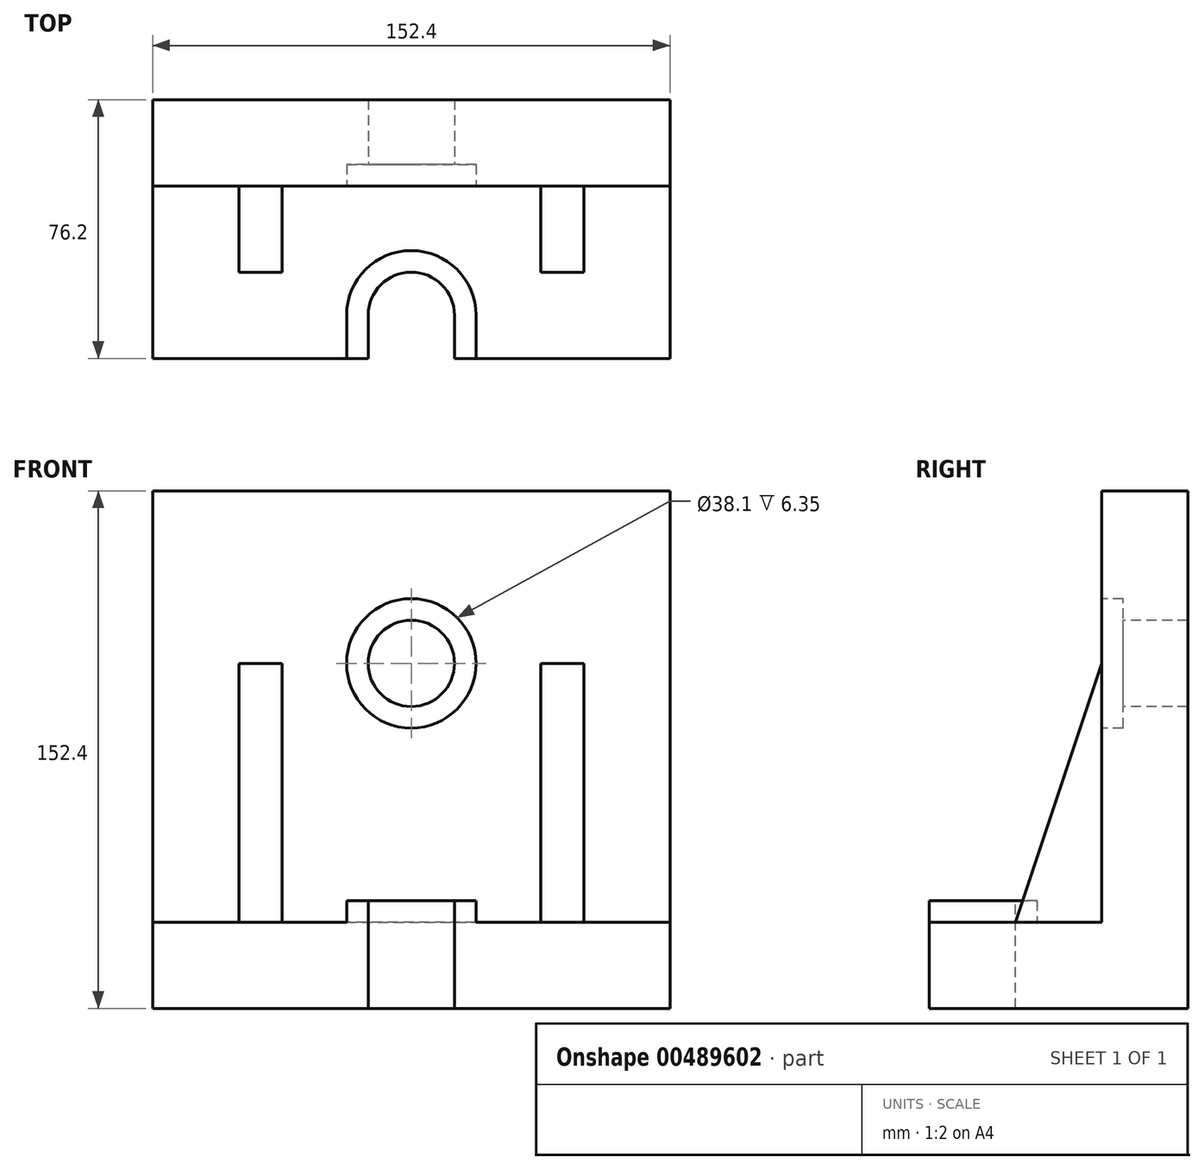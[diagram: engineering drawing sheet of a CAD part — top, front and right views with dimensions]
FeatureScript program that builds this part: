
annotation { "Feature Type Name" : "Feature", "Feature Type Description" : "" }
export const myFeature = defineFeature(function(context is Context, id is Id, definition is map)
    precondition{}
    {
        {
            var Q0;
            Q0=qCreatedBy(makeId("Right.planeOp"),FACE);
            var sketch = newSketch(context, id + "F0", { "sketchPlane" : qUnion([Q0])});
            skLineSegment(sketch, "E0", {"start": v(0, 0) * mm, "end": v(-76.2, 0) * mm});
            skLineSegment(sketch, "E1", {"start": v(-76.2, 0) * mm, "end": v(-76.2, 25.4) * mm});
            skLineSegment(sketch, "E2", {"start": v(-76.2, 25.4) * mm, "end": v(-25.4, 25.4) * mm});
            skLineSegment(sketch, "E3", {"start": v(-25.4, 25.4) * mm, "end": v(-25.4, 152.4) * mm});
            skLineSegment(sketch, "E4", {"start": v(-25.4, 152.4) * mm, "end": v(0, 152.4) * mm});
            skLineSegment(sketch, "E5", {"start": v(0, 152.4) * mm, "end": v(0, 0) * mm});
            skSolve(sketch);
        }
        {
            var Q0;
            Q0 = qSketchRegion(id + "F0", true);
            extrude(context, id + "F1", {"entities" : qUnion([Q0]), "endBound" : BoundingType.SYMMETRIC, "depth" : 152.4 * mm});
        }
        {
            var Q0;
            Q0=makeQuery(id+"F1.opExtrude","SWEPT_FACE",FACE,{"disambiguationData":[OSD([sQuery(id+"F0.wireOp",EDGE,"E2")])]});
            var sketch = newSketch(context, id + "F2", { "sketchPlane" : qUnion([Q0])});
            skArc(sketch, "E6", {"start": v(12.7, -63.5) * mm, "mid": v(0, -50.8) * mm, "end": v(-12.7, -63.5) * mm});
            skPoint(sketch, "E6.centerSnap0", {"position": v(0, -76.2) * mm});
            skLineSegment(sketch, "E7", {"start": v(-12.7, -63.5) * mm, "end": v(-12.7, -76.2) * mm});
            skLineSegment(sketch, "E8", {"start": v(12.7, -63.5) * mm, "end": v(12.7, -76.2) * mm});
            skSolve(sketch);
        }
        {
            var Q0;
            Q0 = qSketchRegion(id + "F2", true);
            var Q1;
            Q1=makeQuery(id+"F2.imprint","IMPRINT",FACE,{"disambiguationData":[TD([[makeQuery(id+"F2.imprint","IMPRINT",EDGE,{"derivedFrom":sQuery(id+"F2.wireOp",EDGE,"E6")}),1.0]])]});
            extrude(context, id + "F3", {"entities" : qUnion([Q0, Q1]), "operationType" : NewBodyOperationType.REMOVE, "endBound" : BoundingType.THROUGH_ALL, "oppositeDirection" : true, "depth" : 25.4 * mm});
        }
        {
            var Q0;
            Q0=makeQuery(id+"F1.opExtrude","SWEPT_FACE",FACE,{"disambiguationData":[OSD([sQuery(id+"F0.wireOp",EDGE,"E3")])]});
            var sketch = newSketch(context, id + "F4", { "sketchPlane" : qUnion([Q0])});
            skCircle(sketch, "E9", {"center": v(0, 101.6) * mm, "radius": 19.05 * mm});
            skCircle(sketch, "E10", {"center": v(0, 101.6) * mm, "radius": 12.7 * mm});
            skSolve(sketch);
        }
        {
            var Q0;
            Q0=makeQuery(id+"F4.imprint","IMPRINT",FACE,{"disambiguationData":[TD([[makeQuery(id+"F4.imprint","IMPRINT",EDGE,{"derivedFrom":sQuery(id+"F4.wireOp",EDGE,"E10")}),1.0]])]});
            extrude(context, id + "F5", {"entities" : qUnion([Q0]), "operationType" : NewBodyOperationType.REMOVE, "endBound" : BoundingType.THROUGH_ALL, "oppositeDirection" : true, "depth" : 25.4 * mm});
        }
        {
            var Q0;
            Q0=makeQuery(id+"F4.imprint","IMPRINT",FACE,{"disambiguationData":[TD([[makeQuery(id+"F4.imprint","IMPRINT",EDGE,{"derivedFrom":sQuery(id+"F4.wireOp",EDGE,"E9")}),1.0]])]});
            extrude(context, id + "F6", {"entities" : qUnion([Q0]), "operationType" : NewBodyOperationType.REMOVE, "oppositeDirection" : true, "depth" : 6.35 * mm});
        }
        {
            var Q0;
            Q0=qCreatedBy(makeId("Right.planeOp"),FACE);
            cPlane(context, id + "F7", {"entities" : qUnion([Q0]), "cplaneType" : CPlaneType.OFFSET, "offset" : 44.45 * mm, "width" : 152.4 * mm, "height" : 152.4 * mm});
        }
        {
            var Q0;
            Q0=qCreatedBy(id+"F7.planeOp",FACE);
            var sketch = newSketch(context, id + "F8", { "sketchPlane" : qUnion([Q0])});
            skLineSegment(sketch, "E11.0", {"start": v(-25.4, 25.4) * mm, "end": v(-25.4, 101.6) * mm});
            skLineSegment(sketch, "E12.0", {"start": v(-76.2, 25.4) * mm, "end": v(-25.4, 25.4) * mm});
            skLineSegment(sketch, "E13", {"start": v(-25.4, 101.6) * mm, "end": v(-50.8, 25.4) * mm});
            skLineSegment(sketch, "E14", {"start": v(-50.8, 25.4) * mm, "end": v(-25.4, 25.4) * mm});
            skSolve(sketch);
        }
        {
            var Q0;
            Q0 = qSketchRegion(id + "F8", true);
            extrude(context, id + "F9", {"entities" : qUnion([Q0]), "endBound" : BoundingType.SYMMETRIC, "depth" : 12.7 * mm});
        }
        {
            var Q0;
            Q0=makeQuery(id+"F9.opExtrude","SWEPT_BODY",BODY,{"disambiguationData":[OSD([sQuery(id+"F8.wireOp",EDGE,"E11.0"),sQuery(id+"F8.wireOp",EDGE,"E13"),sQuery(id+"F8.wireOp",EDGE,"E14")])]});
            var Q1;
            Q1=qCreatedBy(makeId("Right.planeOp"),FACE);
            mirror(context, id + "F10", {"operationType" : NewBodyOperationType.ADD, "entities" : qUnion([Q0]), "mirrorPlane" : qUnion([Q1])});
        }
        {
            var Q0;
            {var subQ2=sQuery(id+"F0.wireOp",EDGE,"E1");Q0=makeQuery(id+"F3.boolean.opBoolean","SPLIT",FACE,{"disambiguationData":[TD([makeQuery(id+"F3.opExtrude","SWEPT_FACE",FACE,{"disambiguationData":[OSD([sQuery(id+"F2.wireOp",EDGE,"E7")])]})])],"derivedFrom":makeQuery(id+"F1.opExtrude","SWEPT_FACE",FACE,{"disambiguationData":[OSD([subQ2])]})});}
            var sketch = newSketch(context, id + "F11", { "sketchPlane" : qUnion([Q0])});
            skLineSegment(sketch, "E15.bottom", {"start": v(-12.7, 25.4) * mm, "end": v(-19.05, 25.4) * mm});
            skLineSegment(sketch, "E15.top", {"start": v(-12.7, 31.75) * mm, "end": v(-19.05, 31.75) * mm});
            skLineSegment(sketch, "E15.left", {"start": v(-12.7, 25.4) * mm, "end": v(-12.7, 31.75) * mm});
            skLineSegment(sketch, "E15.right", {"start": v(-19.05, 25.4) * mm, "end": v(-19.05, 31.75) * mm});
            skSolve(sketch);
        }
        {
            var Q0;
            Q0 = qSketchRegion(id + "F11", true);
            var Q1;
            Q1=sQuery(id+"F2.wireOp",EDGE,"E7");
            var Q2;
            Q2=sQuery(id+"F2.wireOp",EDGE,"E6");
            var Q3;
            Q3=sQuery(id+"F2.wireOp",EDGE,"E8");
            sweep(context, id + "F12", {"operationType" : NewBodyOperationType.ADD, "profiles" : qUnion([Q0]), "path" : qUnion([Q1, Q2, Q3])});
        }
    });
